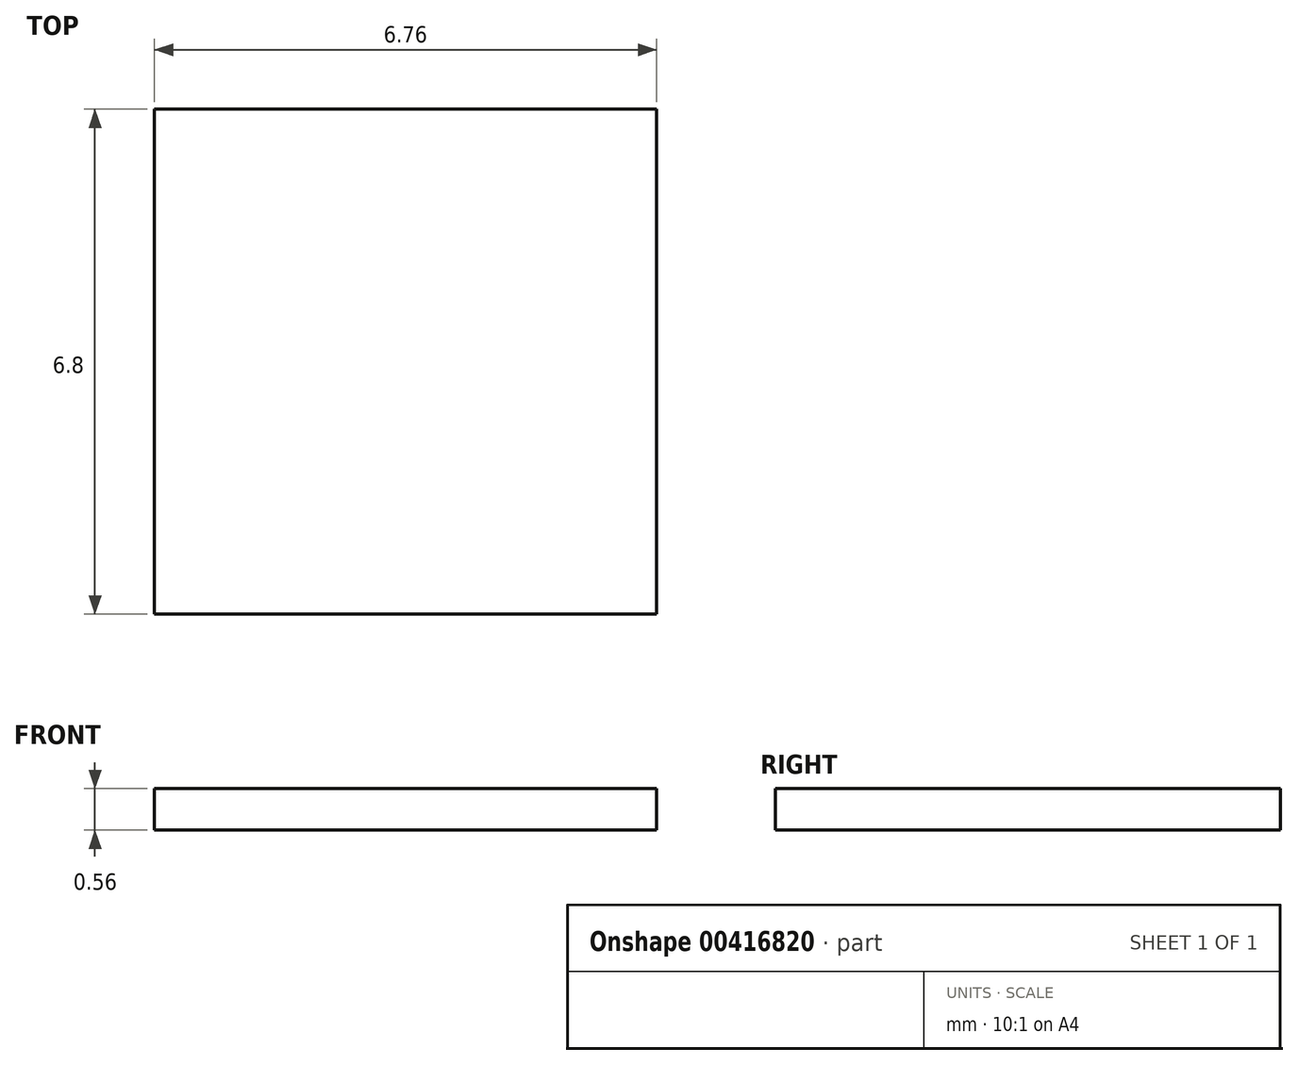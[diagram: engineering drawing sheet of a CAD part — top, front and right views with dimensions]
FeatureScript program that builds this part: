
annotation { "Feature Type Name" : "Feature", "Feature Type Description" : "" }
export const myFeature = defineFeature(function(context is Context, id is Id, definition is map)
    precondition{}
    {
        {
            var Q0;
            Q0=qCreatedBy(makeId("Top.planeOp"),FACE);
            var sketch = newSketch(context, id + "F0", { "sketchPlane" : qUnion([Q0])});
            skLineSegment(sketch, "E0.bottom", {"start": v(0, 0) * mm, "end": v(6.76, 0) * mm});
            skLineSegment(sketch, "E0.top", {"start": v(0, 6.8) * mm, "end": v(6.76, 6.8) * mm});
            skLineSegment(sketch, "E0.left", {"start": v(0, 0) * mm, "end": v(0, 6.8) * mm});
            skLineSegment(sketch, "E0.right", {"start": v(6.76, 0) * mm, "end": v(6.76, 6.8) * mm});
            skSolve(sketch);
        }
        {
            var Q0;
            Q0 = qSketchRegion(id + "F0", true);
            extrude(context, id + "F1", {"entities" : qUnion([Q0]), "depth" : .56 * mm, "offsetDistance" : 25.4 * mm});
        }
    });
